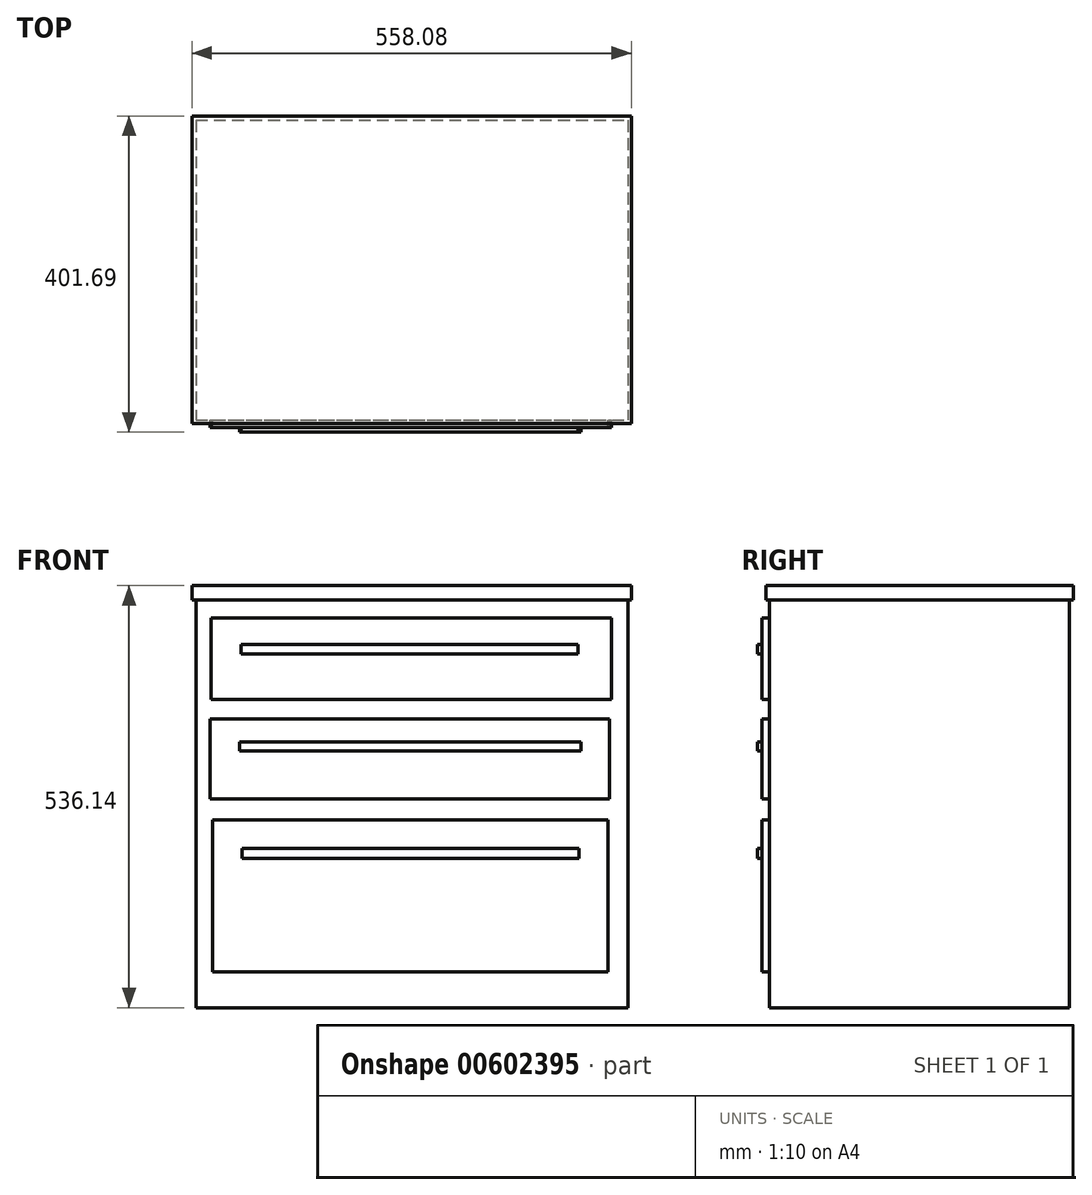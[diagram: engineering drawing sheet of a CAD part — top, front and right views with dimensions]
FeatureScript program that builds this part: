
annotation { "Feature Type Name" : "Feature", "Feature Type Description" : "" }
export const myFeature = defineFeature(function(context is Context, id is Id, definition is map)
    precondition{}
    {
        {
            var Q0;
            Q0=qCreatedBy(makeId("Top.planeOp"),FACE);
            var sketch = newSketch(context, id + "F0", { "sketchPlane" : qUnion([Q0])});
            skLineSegment(sketch, "E0.bottom", {"start": v(-274.32, 190.5) * mm, "end": v(274.32, 190.5) * mm});
            skLineSegment(sketch, "E0.top", {"start": v(-274.32, -190.5) * mm, "end": v(274.32, -190.5) * mm});
            skLineSegment(sketch, "E0.left", {"start": v(-274.32, 190.5) * mm, "end": v(-274.32, -190.5) * mm});
            skLineSegment(sketch, "E0.right", {"start": v(274.32, 190.5) * mm, "end": v(274.32, -190.5) * mm});
            skPoint(sketch, "E0.middle", {"position": v(0, 0) * mm});
            skSolve(sketch);
        }
        {
            var Q0;
            Q0=makeQuery(id+"F0.imprint","IMPRINT",FACE,{"disambiguationData":[TD([[makeQuery(id+"F0.imprint","IMPRINT",EDGE,{"derivedFrom":sQuery(id+"F0.wireOp",EDGE,"E0.bottom")}),-1.0]])]});
            extrude(context, id + "F1", {"entities" : qUnion([Q0]), "depth" : 518.16 * mm, "offsetDistance" : 30.48 * mm});
        }
        {
            var Q0;
            Q0=makeQuery(id+"F1.opExtrude","CAP_FACE",FACE,{"disambiguationData":[OSD([sQuery(id+"F0.wireOp",EDGE,"E0.bottom"),sQuery(id+"F0.wireOp",EDGE,"E0.top"),sQuery(id+"F0.wireOp",EDGE,"E0.left"),sQuery(id+"F0.wireOp",EDGE,"E0.right")])],"isStart":false});
            var sketch = newSketch(context, id + "F2", { "sketchPlane" : qUnion([Q0])});
            skLineSegment(sketch, "E1.bottom", {"start": v(-279.28, -194.92) * mm, "end": v(278.8, -194.92) * mm});
            skLineSegment(sketch, "E1.top", {"start": v(-279.28, 195.95) * mm, "end": v(278.8, 195.95) * mm});
            skLineSegment(sketch, "E1.left", {"start": v(-279.28, -194.92) * mm, "end": v(-279.28, 195.95) * mm});
            skLineSegment(sketch, "E1.right", {"start": v(278.8, -194.92) * mm, "end": v(278.8, 195.95) * mm});
            skSolve(sketch);
        }
        {
            var Q0;
            Q0=makeQuery(id+"F2.imprint","IMPRINT",FACE,{"disambiguationData":[TD([[makeQuery(id+"F2.imprint","IMPRINT",EDGE,{"derivedFrom":sQuery(id+"F2.wireOp",EDGE,"E1.bottom")}),1.0]])]});
            var Q1;
            Q1=makeQuery(id+"F2.imprint","IMPRINT",FACE,{"disambiguationData":[TD([[makeQuery(id+"F2.imprint","IMPRINT",EDGE,{"derivedFrom":makeQuery(id+"F1.opExtrude","CAP_EDGE",EDGE,{"disambiguationData":[OSD([sQuery(id+"F0.wireOp",EDGE,"E0.bottom")])],"isStart":false})}),-1.0]])]});
            extrude(context, id + "F3", {"entities" : qUnion([Q0, Q1]), "operationType" : NewBodyOperationType.ADD, "depth" : 17.98 * mm, "offsetDistance" : 30.48 * mm});
        }
        {
            var Q0;
            Q0=makeQuery(id+"F1.opExtrude","SWEPT_FACE",FACE,{"disambiguationData":[OSD([sQuery(id+"F0.wireOp",EDGE,"E0.top")])]});
            var sketch = newSketch(context, id + "F4", { "sketchPlane" : qUnion([Q0])});
            skLineSegment(sketch, "E2.bottom", {"start": v(-255.23, 495.37) * mm, "end": v(253.59, 495.37) * mm});
            skLineSegment(sketch, "E2.top", {"start": v(-255.23, 391.29) * mm, "end": v(253.59, 391.29) * mm});
            skLineSegment(sketch, "E2.left", {"start": v(-255.23, 495.37) * mm, "end": v(-255.23, 391.29) * mm});
            skLineSegment(sketch, "E2.right", {"start": v(253.59, 495.37) * mm, "end": v(253.59, 391.29) * mm});
            skSolve(sketch);
        }
        {
            var Q0;
            Q0=makeQuery(id+"F4.imprint","IMPRINT",FACE,{"disambiguationData":[TD([[makeQuery(id+"F4.imprint","IMPRINT",EDGE,{"derivedFrom":sQuery(id+"F4.wireOp",EDGE,"E2.bottom")}),1.0]])]});
            var sketch = newSketch(context, id + "F5", { "sketchPlane" : qUnion([Q0])});
            skLineSegment(sketch, "E3.bottom", {"start": v(-256.39, 367) * mm, "end": v(251.27, 367) * mm});
            skLineSegment(sketch, "E3.top", {"start": v(-256.39, 265.24) * mm, "end": v(251.27, 265.24) * mm});
            skLineSegment(sketch, "E3.left", {"start": v(-256.39, 367) * mm, "end": v(-256.39, 265.24) * mm});
            skLineSegment(sketch, "E3.right", {"start": v(251.27, 367) * mm, "end": v(251.27, 265.24) * mm});
            skSolve(sketch);
        }
        {
            var Q0;
            Q0=makeQuery(id+"F4.imprint","IMPRINT",FACE,{"disambiguationData":[TD([[makeQuery(id+"F4.imprint","IMPRINT",EDGE,{"derivedFrom":sQuery(id+"F4.wireOp",EDGE,"E2.bottom")}),1.0]])]});
            var sketch = newSketch(context, id + "F6", { "sketchPlane" : qUnion([Q0])});
            skLineSegment(sketch, "E4.bottom", {"start": v(-252.92, 238.64) * mm, "end": v(248.96, 238.64) * mm});
            skLineSegment(sketch, "E4.top", {"start": v(-252.92, 45.53) * mm, "end": v(248.96, 45.53) * mm});
            skLineSegment(sketch, "E4.left", {"start": v(-252.92, 238.64) * mm, "end": v(-252.92, 45.53) * mm});
            skLineSegment(sketch, "E4.right", {"start": v(248.96, 238.64) * mm, "end": v(248.96, 45.53) * mm});
            skSolve(sketch);
        }
        {
            var Q0;
            Q0=makeQuery(id+"F4.imprint","IMPRINT",FACE,{"disambiguationData":[TD([[makeQuery(id+"F4.imprint","IMPRINT",EDGE,{"derivedFrom":sQuery(id+"F4.wireOp",EDGE,"E2.bottom")}),-1.0]])]});
            var Q1;
            Q1=makeQuery(id+"F5.imprint","IMPRINT",FACE,{"disambiguationData":[TD([[makeQuery(id+"F5.imprint","IMPRINT",EDGE,{"derivedFrom":sQuery(id+"F5.wireOp",EDGE,"E3.bottom")}),-1.0]])]});
            var Q2;
            Q2=makeQuery(id+"F6.imprint","IMPRINT",FACE,{"disambiguationData":[TD([[makeQuery(id+"F6.imprint","IMPRINT",EDGE,{"derivedFrom":sQuery(id+"F6.wireOp",EDGE,"E4.bottom")}),-1.0]])]});
            extrude(context, id + "F7", {"entities" : qUnion([Q0, Q1, Q2]), "operationType" : NewBodyOperationType.ADD, "depth" : 9.14 * mm, "offsetDistance" : 30.48 * mm});
        }
        {
            var Q0;
            Q0=makeQuery(id+"F7.opExtrude","CAP_FACE",FACE,{"disambiguationData":[OSD([sQuery(id+"F4.wireOp",EDGE,"E2.bottom"),sQuery(id+"F4.wireOp",EDGE,"E2.top"),sQuery(id+"F4.wireOp",EDGE,"E2.left"),sQuery(id+"F4.wireOp",EDGE,"E2.right")])],"isStart":false});
            var sketch = newSketch(context, id + "F8", { "sketchPlane" : qUnion([Q0])});
            skLineSegment(sketch, "E5.bottom", {"start": v(-216.57, 461.59) * mm, "end": v(211.12, 461.59) * mm});
            skLineSegment(sketch, "E5.top", {"start": v(-216.57, 449.2) * mm, "end": v(211.12, 449.2) * mm});
            skLineSegment(sketch, "E5.left", {"start": v(-216.57, 461.59) * mm, "end": v(-216.57, 449.2) * mm});
            skLineSegment(sketch, "E5.right", {"start": v(211.12, 461.59) * mm, "end": v(211.12, 449.2) * mm});
            skSolve(sketch);
        }
        {
            var Q0;
            Q0=makeQuery(id+"F7.opExtrude","CAP_FACE",FACE,{"disambiguationData":[OSD([sQuery(id+"F5.wireOp",EDGE,"E3.bottom"),sQuery(id+"F5.wireOp",EDGE,"E3.top"),sQuery(id+"F5.wireOp",EDGE,"E3.left"),sQuery(id+"F5.wireOp",EDGE,"E3.right")])],"isStart":false});
            var sketch = newSketch(context, id + "F9", { "sketchPlane" : qUnion([Q0])});
            skLineSegment(sketch, "E6.bottom", {"start": v(-218.8, 337.5) * mm, "end": v(214.58, 337.5) * mm});
            skLineSegment(sketch, "E6.top", {"start": v(-218.8, 326.05) * mm, "end": v(214.58, 326.05) * mm});
            skLineSegment(sketch, "E6.left", {"start": v(-218.8, 337.5) * mm, "end": v(-218.8, 326.05) * mm});
            skLineSegment(sketch, "E6.right", {"start": v(214.58, 337.5) * mm, "end": v(214.58, 326.05) * mm});
            skSolve(sketch);
        }
        {
            var Q0;
            Q0=makeQuery(id+"F7.opExtrude","CAP_FACE",FACE,{"disambiguationData":[OSD([sQuery(id+"F6.wireOp",EDGE,"E4.bottom"),sQuery(id+"F6.wireOp",EDGE,"E4.top"),sQuery(id+"F6.wireOp",EDGE,"E4.left"),sQuery(id+"F6.wireOp",EDGE,"E4.right")])],"isStart":false});
            var sketch = newSketch(context, id + "F10", { "sketchPlane" : qUnion([Q0])});
            skLineSegment(sketch, "E7.bottom", {"start": v(-215.63, 202.04) * mm, "end": v(212.23, 202.04) * mm});
            skLineSegment(sketch, "E7.top", {"start": v(-215.63, 189.4) * mm, "end": v(212.23, 189.4) * mm});
            skLineSegment(sketch, "E7.left", {"start": v(-215.63, 202.04) * mm, "end": v(-215.63, 189.4) * mm});
            skLineSegment(sketch, "E7.right", {"start": v(212.23, 202.04) * mm, "end": v(212.23, 189.4) * mm});
            skSolve(sketch);
        }
        {
            var Q0;
            Q0=makeQuery(id+"F10.imprint","IMPRINT",FACE,{"disambiguationData":[TD([[makeQuery(id+"F10.imprint","IMPRINT",EDGE,{"derivedFrom":sQuery(id+"F10.wireOp",EDGE,"E7.bottom")}),-1.0]])]});
            var Q1;
            Q1=makeQuery(id+"F9.imprint","IMPRINT",FACE,{"disambiguationData":[TD([[makeQuery(id+"F9.imprint","IMPRINT",EDGE,{"derivedFrom":sQuery(id+"F9.wireOp",EDGE,"E6.bottom")}),-1.0]])]});
            var Q2;
            Q2=makeQuery(id+"F8.imprint","IMPRINT",FACE,{"disambiguationData":[TD([[makeQuery(id+"F8.imprint","IMPRINT",EDGE,{"derivedFrom":sQuery(id+"F8.wireOp",EDGE,"E5.bottom")}),-1.0]])]});
            extrude(context, id + "F11", {"entities" : qUnion([Q0, Q1, Q2]), "operationType" : NewBodyOperationType.ADD, "depth" : 6.1 * mm, "offsetDistance" : 30.48 * mm});
        }
    });
